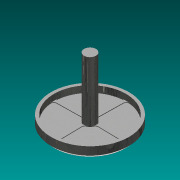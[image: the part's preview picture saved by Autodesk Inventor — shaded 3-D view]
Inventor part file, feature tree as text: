
AUTODESK INVENTOR PART (.ipt)
format: ipt  version: 2021 (Build 250183000, 183)  size: 275,456 bytes
history: native  units: mm
features: sketch x9, extrude x5, sweep x2, fillet x1, pattern_circular x1, other x1
ambient origin geometry x8: Origin, YZ Plane, XZ Plane, XY Plane, X Axis, Y Axis, Z Axis, Center Point
bodies: 实体1 (feature_tree)
feature tree (19):
  extrude  "拉伸1"  Depth=30.0mm TaperAngle=0.0deg
  sweep  "扫掠1"
  sweep  "扫掠2"
  extrude  "拉伸2"  Depth=10.0mm
  fillet  "圆角1"  Radius=10.0mm
  pattern_circular  "环形阵列1"  [2 undecoded]
  extrude  "拉伸3"  Depth=50.0mm
  extrude  "拉伸4"  Depth=600.0mm
  sketch  "草图8"  dims[d17=5.0mm]
  sketch  "草图9"  dims[d18=5.0mm d19=0.0mm d20=0.0mm d22=200.0mm d24=600.0mm d25=15.882496mm d26=1200.0mm d27=10.0mm d28=0.0mm d29=50.0mm d30=40.0mm d31=360.0deg d33=100.0mm d34=0.0mm d35=200.0mm d36=1000.0mm d37=0.0mm d38=30.0mm d39=50.0mm d40=0.0mm d41=0.5mm d42=0.872665mm]
  extrude  "拉伸5"  Depth=50.0mm
  sketch  "草图1"  dims[d0=1300.0mm d1=30.0mm d2=0.0mm]
  sketch  "草图2"  dims[d3=30.0mm d4=30.0mm]
  sketch  "草图3"  dims[d7=50.0mm d8=1200.0mm]
  sketch  "草图4"  dims[d9=0.0mm d10=0.0mm d12=10.0mm d13=10.0mm]
  other  "三维草图1"
  sketch  "草图5"  dims[d14=5.0mm]
  sketch  "草图6"  dims[d15=5.0mm]
  sketch  "草图7"  dims[d16=5.0mm]
note: 2 required parameter values undecoded (feature->parameter linkage not recoverable at this tier; creation-order binding heuristic only, values carry confidence <= 0.55)
